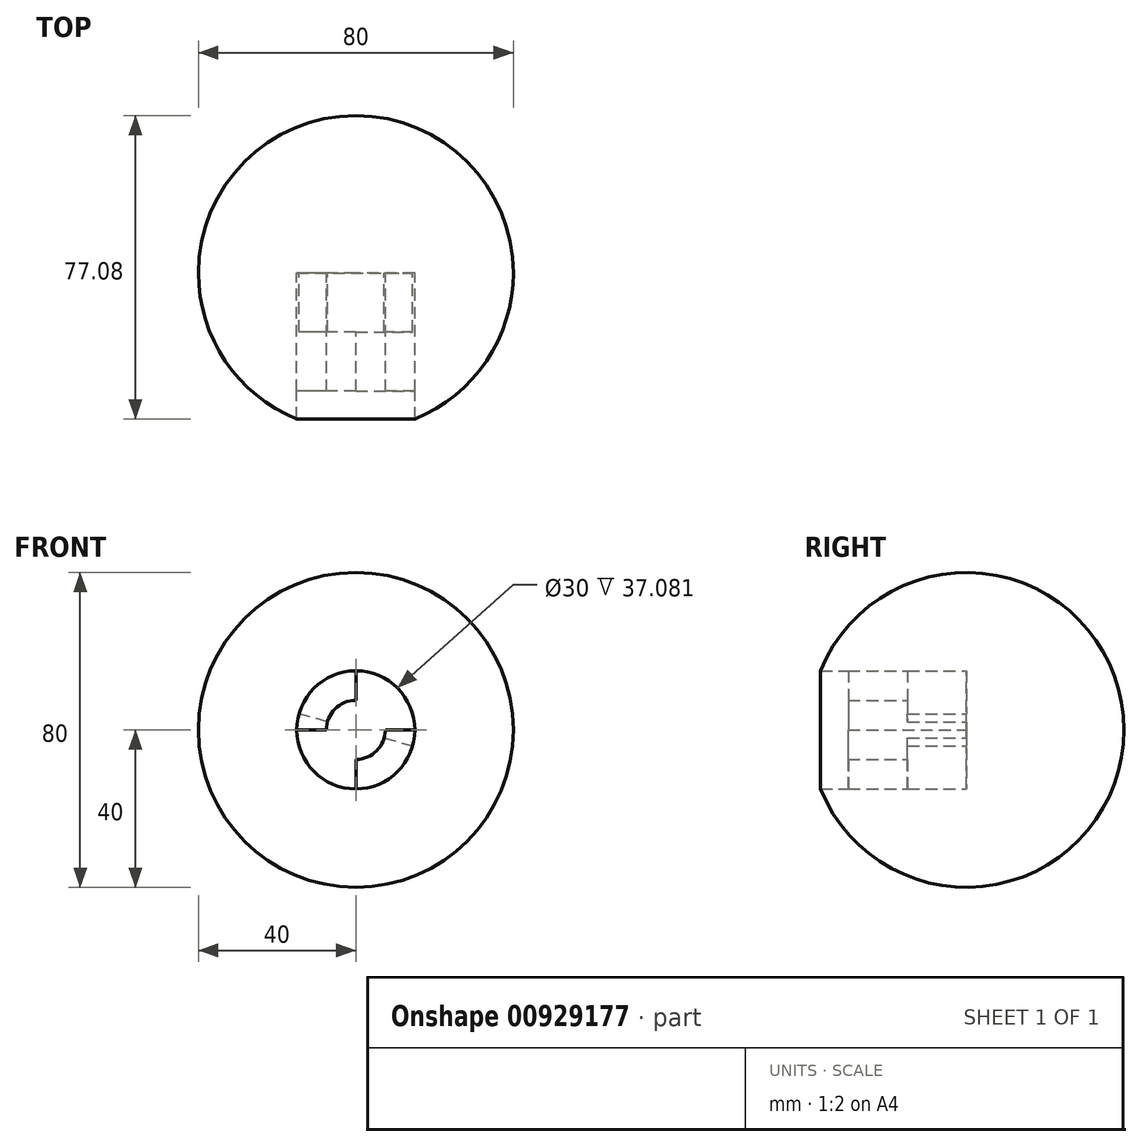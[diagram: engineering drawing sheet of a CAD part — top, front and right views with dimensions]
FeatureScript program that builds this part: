
annotation { "Feature Type Name" : "Feature", "Feature Type Description" : "" }
export const myFeature = defineFeature(function(context is Context, id is Id, definition is map)
    precondition{}
    {
        {
            var Q0;
            Q0=qCreatedBy(makeId("Top.planeOp"),FACE);
            var sketch = newSketch(context, id + "F0", { "sketchPlane" : qUnion([Q0])});
            skArc(sketch, "E0", {"start": v(-40, 0) * mm, "mid": v(0, -40) * mm, "end": v(40, 0) * mm});
            skLineSegment(sketch, "E1", {"start": v(-40, 0) * mm, "end": v(40, 0) * mm});
            skSolve(sketch);
        }
        {
            var Q0;
            Q0=qCreatedBy(makeId("Front.planeOp"),FACE);
            var sketch = newSketch(context, id + "F1", { "sketchPlane" : qUnion([Q0])});
            skCircle(sketch, "E2", {"center": v(0, 0) * mm, "radius": 15 * mm});
            skArc(sketch, "E3", {"start": v(0, -7.5) * mm, "mid": v(5.3, -5.3) * mm, "end": v(7.5, 0) * mm});
            skLineSegment(sketch, "E4", {"start": v(0, 15) * mm, "end": v(0, 7.5) * mm});
            skLineSegment(sketch, "E5", {"start": v(15, 0) * mm, "end": v(7.5, 0) * mm});
            skLineSegment(sketch, "E6.trimOffspring", {"start": v(0, -7.5) * mm, "end": v(0, -15) * mm});
            skLineSegment(sketch, "E7.trimOffspring", {"start": v(-7.5, 0) * mm, "end": v(-15, 0) * mm});
            skArc(sketch, "E8.trimOffspring", {"start": v(0, 7.5) * mm, "mid": v(-5.3, 5.3) * mm, "end": v(-7.5, 0) * mm});
            skLineSegment(sketch, "E9", {"start": v(0, 0) * mm, "end": v(-14.43, 4.1) * mm});
            skLineSegment(sketch, "E10", {"start": v(-14.43, 4.1) * mm, "end": v(14.43, -4.1) * mm});
            skSolve(sketch);
        }
        {
            var Q0;
            Q0=makeQuery(id+"F0.imprint","IMPRINT",FACE,{"disambiguationData":[TD([[makeQuery(id+"F0.imprint","IMPRINT",EDGE,{"derivedFrom":sQuery(id+"F0.wireOp",EDGE,"E0")}),1.0]])]});
            var Q1;
            Q1=sQuery(id+"F0.wireOp",EDGE,"E1");
            revolve(context, id + "F2", {"surfaceOperationType" : NewSurfaceOperationType.NEW, "entities" : qUnion([Q0]), "axis" : qUnion([Q1]), "revolveType" : RevolveType.FULL});
        }
        {
            var Q0;
            Q0=qSketchRegion(id+"F1",true);
            extrude(context, id + "F3", {"entities" : qUnion([Q0]), "operationType" : NewBodyOperationType.REMOVE, "depth" : 100 * mm, "offsetDistance" : 25 * mm});
        }
        {
            var Q0;
            {var subQ0=sQuery(id+"F1.wireOp",EDGE,"E4");Q0=makeQuery(id+"F1.imprint","IMPRINT",FACE,{"disambiguationData":[TD([[makeQuery(id+"F1.imprint","IMPRINT",EDGE,{"derivedFrom":subQ0}),-1.0]])]});}
            var Q1;
            Q1=makeQuery(id+"F1.imprint","IMPRINT",FACE,{"disambiguationData":[TD([[makeQuery(id+"F1.imprint","IMPRINT",EDGE,{"derivedFrom":sQuery(id+"F1.wireOp",EDGE,"E3")}),-1.0]])]});
            extrude(context, id + "F4", {"entities" : qUnion([Q0, Q1]), "operationType" : NewBodyOperationType.ADD, "depth" : 30 * mm, "offsetDistance" : 25 * mm});
        }
        {
            var Q0;
            {var subQ0=sQuery(id+"F1.wireOp",EDGE,"E4");Q0=makeQuery(id+"F1.imprint","IMPRINT",FACE,{"disambiguationData":[TD([[makeQuery(id+"F1.imprint","IMPRINT",EDGE,{"derivedFrom":subQ0}),-1.0]])]});}
            var Q1;
            Q1=makeQuery(id+"F1.imprint","IMPRINT",FACE,{"disambiguationData":[TD([[makeQuery(id+"F1.imprint","IMPRINT",EDGE,{"derivedFrom":sQuery(id+"F1.wireOp",EDGE,"E3")}),-1.0]])]});
            extrude(context, id + "F5", {"entities" : qUnion([Q0, Q1]), "operationType" : NewBodyOperationType.REMOVE, "depth" : 15 * mm, "offsetDistance" : 25 * mm});
        }
        {
            var Q0;
            {var subQ0=sQuery(id+"F1.wireOp",EDGE,"E7.trimOffspring");Q0=makeQuery(id+"F1.imprint","IMPRINT",FACE,{"disambiguationData":[TD([[makeQuery(id+"F1.imprint","IMPRINT",EDGE,{"derivedFrom":subQ0}),-1.0]])]});}
            var Q1;
            {var subQ0=sQuery(id+"F1.wireOp",EDGE,"E5");Q1=makeQuery(id+"F1.imprint","IMPRINT",FACE,{"disambiguationData":[TD([[makeQuery(id+"F1.imprint","IMPRINT",EDGE,{"derivedFrom":subQ0}),1.0]])]});}
            extrude(context, id + "F6", {"entities" : qUnion([Q0, Q1]), "operationType" : NewBodyOperationType.ADD, "depth" : 30 * mm, "offsetDistance" : 25 * mm});
        }
    });
